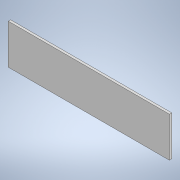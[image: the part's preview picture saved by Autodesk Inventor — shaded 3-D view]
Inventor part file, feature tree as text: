
AUTODESK INVENTOR PART (.ipt)
format: ipt  version: 2021 (Build 250183000, 183)  size: 90,112 bytes
history: native  units: in
note: dims shown in document units (in); Inventor stores cm internally (conversion verified against a paired STEP export)
features: extrude x1, sketch x1
ambient origin geometry x8: Origin, YZ Plane, XZ Plane, XY Plane, X Axis, Y Axis, Z Axis, Center Point
bodies: Solid1 (feature_tree)
feature tree (2):
  extrude  "Extrusion1"  Depth=1.683in
  sketch  "Sketch1"  dims[d0=6.8in d1=1.683in d2=0.1in d3=0.0in]
